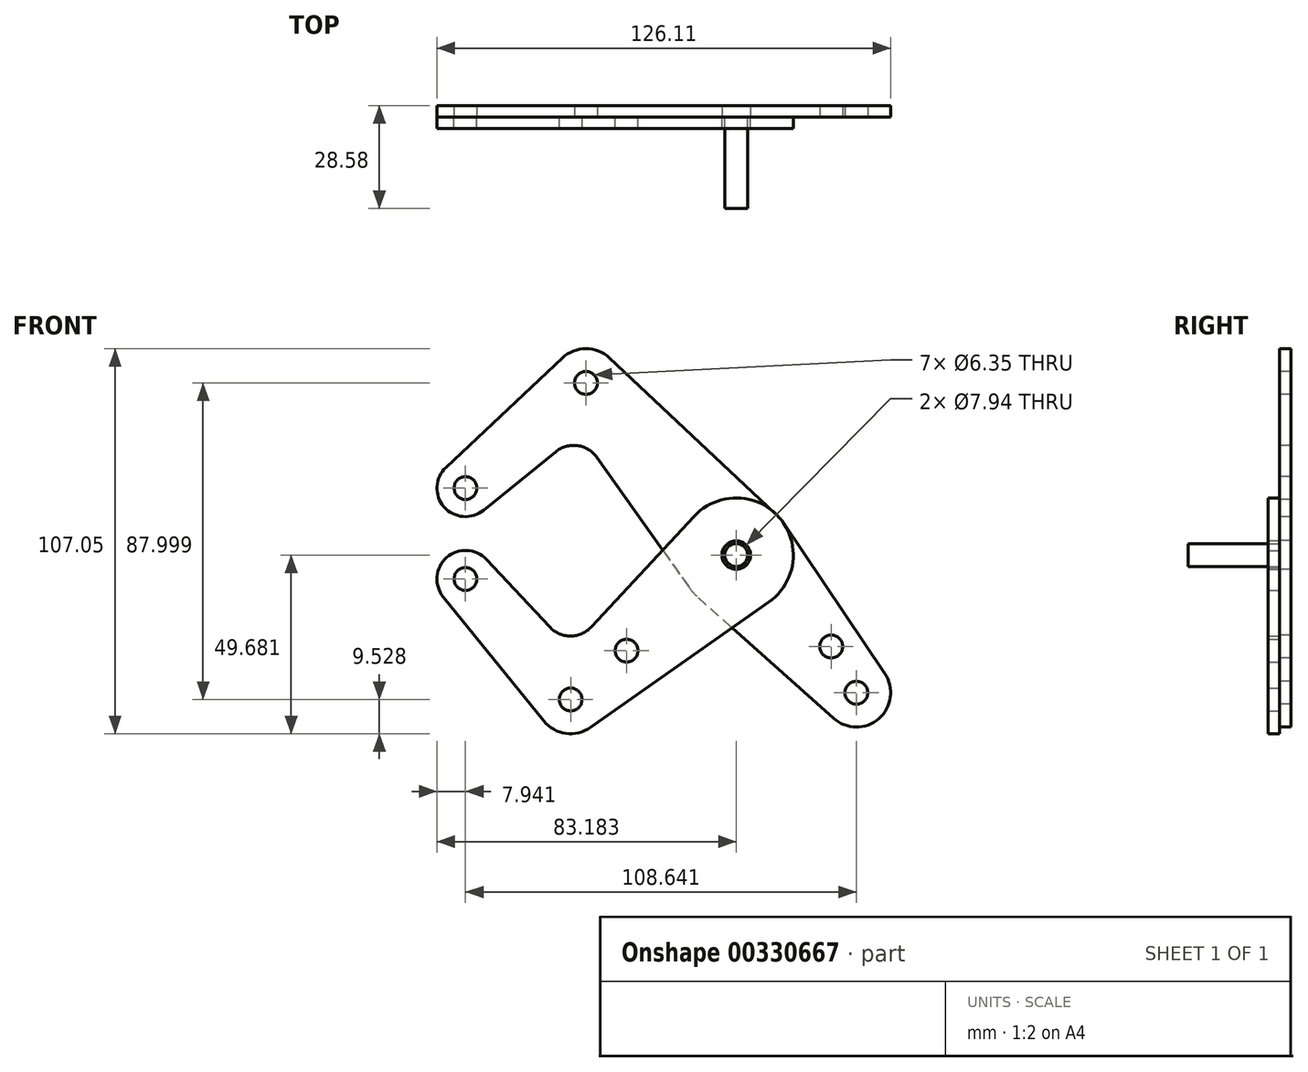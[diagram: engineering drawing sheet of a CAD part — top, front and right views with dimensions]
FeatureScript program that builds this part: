
annotation { "Feature Type Name" : "Feature", "Feature Type Description" : "" }
export const myFeature = defineFeature(function(context is Context, id is Id, definition is map)
    precondition{}
    {
        {
            var Q0;
            Q0=qCreatedBy(makeId("Front.planeOp"),FACE);
            var sketch = newSketch(context, id + "F0", { "sketchPlane" : qUnion([Q0])});
            skLineSegment(sketch, "E0", {"start": v(-8.96, 54.5) * mm, "end": v(73.88, -40.43) * mm, "construction": true});
            skCircle(sketch, "E1", {"center": v(32.8, 6.66) * mm, "radius": 3.18 * mm});
            skCircle(sketch, "E2", {"center": v(66.2, -31.62) * mm, "radius": 3.18 * mm});
            skCircle(sketch, "E3", {"center": v(-8.96, 54.5) * mm, "radius": 3.18 * mm});
            skCircle(sketch, "E4", {"center": v(-42.45, 25.28) * mm, "radius": 3.18 * mm});
            skLineSegment(sketch, "E5", {"start": v(-8.96, 54.5) * mm, "end": v(-42.45, 25.28) * mm, "construction": true});
            skCircle(sketch, "E6", {"center": v(66.2, -31.62) * mm, "radius": 9.53 * mm});
            skCircle(sketch, "E7", {"center": v(-42.45, 25.28) * mm, "radius": 7.94 * mm});
            skCircle(sketch, "E8", {"center": v(-8.96, 54.5) * mm, "radius": 9.53 * mm});
            skLineSegment(sketch, "E9", {"start": v(-47.88, 31.07) * mm, "end": v(-15.47, 61.46) * mm});
            skLineSegment(sketch, "E10", {"start": v(-37.45, 19.12) * mm, "end": v(-17.42, 35.37) * mm});
            skCircle(sketch, "E11", {"center": v(32.8, 6.66) * mm, "radius": 15.88 * mm});
            skLineSegment(sketch, "E12", {"start": v(-2.44, 61.46) * mm, "end": v(43.65, 18.24) * mm});
            skLineSegment(sketch, "E13", {"start": v(-5.94, 33.8) * mm, "end": v(19.85, -2.53) * mm});
            skLineSegment(sketch, "E14", {"start": v(22.23, -5.19) * mm, "end": v(59.85, -38.73) * mm});
            skLineSegment(sketch, "E15", {"start": v(45.97, 15.52) * mm, "end": v(74.1, -26.3) * mm});
            skArc(sketch, "E16.filletArc", {"start": v(-5.94, 33.8) * mm, "mid": v(-11.34, 37.08) * mm, "end": v(-17.42, 35.37) * mm});
            skLineSegment(sketch, "E17", {"start": v(34.62, 8.26) * mm, "end": v(-13.22, -33.5) * mm, "construction": true});
            skLineSegment(sketch, "E18", {"start": v(-13.22, -33.5) * mm, "end": v(-42.45, 0) * mm, "construction": true});
            skCircle(sketch, "E19", {"center": v(-42.45, 0) * mm, "radius": 3.18 * mm});
            skCircle(sketch, "E20", {"center": v(-13.22, -33.5) * mm, "radius": 3.18 * mm});
            skCircle(sketch, "E21", {"center": v(-42.45, 0) * mm, "radius": 7.94 * mm});
            skCircle(sketch, "E22", {"center": v(-13.22, -33.5) * mm, "radius": 9.53 * mm});
            skLineSegment(sketch, "E23", {"start": v(-36.66, 5.43) * mm, "end": v(-19.07, -13.34) * mm});
            skLineSegment(sketch, "E24", {"start": v(-48.61, -5) * mm, "end": v(-20.62, -39.5) * mm});
            skLineSegment(sketch, "E25", {"start": v(21.17, 17.47) * mm, "end": v(-7.46, -13.31) * mm});
            skLineSegment(sketch, "E26", {"start": v(41.93, -6.32) * mm, "end": v(-7.74, -41.28) * mm});
            skArc(sketch, "E27.filletArc", {"start": v(-19.07, -13.34) * mm, "mid": v(-13.26, -15.84) * mm, "end": v(-7.46, -13.31) * mm});
            skCircle(sketch, "E28", {"center": v(2.33, -19.92) * mm, "radius": 3.18 * mm});
            skCircle(sketch, "E29", {"center": v(59.2, -18.76) * mm, "radius": 3.18 * mm});
            skLineSegment(sketch, "E30", {"start": v(59.2, -18.76) * mm, "end": v(56.8, -20.85) * mm, "construction": true});
            skCircle(sketch, "E31", {"center": v(32.8, 6.66) * mm, "radius": 3.97 * mm});
            skLineSegment(sketch, "E32", {"start": v(-7.4, -25.96) * mm, "end": v(-6.39, -40.12) * mm});
            skLineSegment(sketch, "E33", {"start": v(-13.22, -33.5) * mm, "end": v(-6.9, -33.04) * mm});
            skSolve(sketch);
        }
        {
            var Q0;
            {var subQ6=sQuery(id+"F0.wireOp",EDGE,"E9");Q0=makeQuery(id+"F0.imprint","IMPRINT",FACE,{"disambiguationData":[TD([[makeQuery(id+"F0.imprint","IMPRINT",EDGE,{"derivedFrom":subQ6}),-1.0]])]});}
            var Q1;
            Q1=makeQuery(id+"F0.imprint","IMPRINT",FACE,{"disambiguationData":[TD([[makeQuery(id+"F0.imprint","IMPRINT",EDGE,{"derivedFrom":sQuery(id+"F0.wireOp",EDGE,"E3")}),-1.0]])]});
            var Q2;
            Q2=makeQuery(id+"F0.imprint","IMPRINT",FACE,{"disambiguationData":[TD([[makeQuery(id+"F0.imprint","IMPRINT",EDGE,{"derivedFrom":sQuery(id+"F0.wireOp",EDGE,"E4")}),-1.0]])]});
            var Q3;
            Q3=makeQuery(id+"F0.imprint","IMPRINT",FACE,{"disambiguationData":[TD([[makeQuery(id+"F0.imprint","IMPRINT",EDGE,{"derivedFrom":sQuery(id+"F0.wireOp",EDGE,"E31")}),-1.0]])]});
            var Q4;
            {var subQ0=sQuery(id+"F0.wireOp",EDGE,"E15");Q4=makeQuery(id+"F0.imprint","IMPRINT",FACE,{"disambiguationData":[TD([[makeQuery(id+"F0.imprint","IMPRINT",EDGE,{"derivedFrom":subQ0}),-1.0]])]});}
            var Q5;
            {var subQ0=sQuery(id+"F0.wireOp",EDGE,"E14");var subQ1=sQuery(id+"F0.wireOp",EDGE,"E11");var subQ2=makeQuery(id+"F0.imprint","INTERSECT",VERTEX,{"derivedFrom":[subQ1,subQ0]});Q5=makeQuery(id+"F0.imprint","IMPRINT",FACE,{"disambiguationData":[TD([[makeQuery(id+"F0.imprint","IMPRINT",EDGE,{"disambiguationData":[TD([[subQ2,-1.0]])],"derivedFrom":subQ1}),-1.0]])]});}
            var Q6;
            {var subQ0=sQuery(id+"F0.wireOp",EDGE,"E13");var subQ1=sQuery(id+"F0.wireOp",EDGE,"E11");var subQ2=makeQuery(id+"F0.imprint","INTERSECT",VERTEX,{"derivedFrom":[subQ1,subQ0]});Q6=makeQuery(id+"F0.imprint","IMPRINT",FACE,{"disambiguationData":[TD([[makeQuery(id+"F0.imprint","IMPRINT",EDGE,{"disambiguationData":[TD([[subQ2,1.0]])],"derivedFrom":subQ1}),-1.0]])]});}
            var Q7;
            Q7=makeQuery(id+"F0.imprint","IMPRINT",FACE,{"disambiguationData":[TD([[makeQuery(id+"F0.imprint","IMPRINT",EDGE,{"derivedFrom":sQuery(id+"F0.wireOp",EDGE,"E2")}),-1.0]])]});
            var Q8;
            {var subQ0=sQuery(id+"F0.wireOp",EDGE,"E14");var subQ1=sQuery(id+"F0.wireOp",EDGE,"E6");var subQ2=makeQuery(id+"F0.imprint","INTERSECT",VERTEX,{"derivedFrom":[subQ1,subQ0]});Q8=makeQuery(id+"F0.imprint","IMPRINT",FACE,{"disambiguationData":[TD([[makeQuery(id+"F0.imprint","IMPRINT",EDGE,{"disambiguationData":[TD([[subQ2,1.0]])],"derivedFrom":subQ1}),-1.0]])]});}
            extrude(context, id + "F1", {"entities" : qUnion([Q0, Q1, Q2, Q3, Q4, Q5, Q6, Q7, Q8]), "oppositeDirection" : true, "depth" : 3.17 * mm});
        }
        {
            var Q0;
            {var subQ13=sQuery(id+"F0.wireOp",EDGE,"E23");Q0=makeQuery(id+"F0.imprint","IMPRINT",FACE,{"disambiguationData":[TD([[makeQuery(id+"F0.imprint","IMPRINT",EDGE,{"derivedFrom":subQ13}),-1.0]])]});}
            var Q1;
            Q1=makeQuery(id+"F0.imprint","IMPRINT",FACE,{"disambiguationData":[TD([[makeQuery(id+"F0.imprint","IMPRINT",EDGE,{"derivedFrom":sQuery(id+"F0.wireOp",EDGE,"E20")}),-1.0]])]});
            var Q2;
            Q2=makeQuery(id+"F0.imprint","IMPRINT",FACE,{"disambiguationData":[TD([[makeQuery(id+"F0.imprint","IMPRINT",EDGE,{"derivedFrom":sQuery(id+"F0.wireOp",EDGE,"E19")}),-1.0]])]});
            var Q3;
            {var subQ0=sQuery(id+"F0.wireOp",EDGE,"E14");var subQ1=sQuery(id+"F0.wireOp",EDGE,"E11");var subQ2=makeQuery(id+"F0.imprint","INTERSECT",VERTEX,{"derivedFrom":[subQ1,subQ0]});Q3=makeQuery(id+"F0.imprint","IMPRINT",FACE,{"disambiguationData":[TD([[makeQuery(id+"F0.imprint","IMPRINT",EDGE,{"disambiguationData":[TD([[subQ2,-1.0]])],"derivedFrom":subQ1}),-1.0]])]});}
            var Q4;
            Q4=makeQuery(id+"F0.imprint","IMPRINT",FACE,{"disambiguationData":[TD([[makeQuery(id+"F0.imprint","IMPRINT",EDGE,{"derivedFrom":sQuery(id+"F0.wireOp",EDGE,"E31")}),-1.0]])]});
            var Q5;
            {var subQ0=sQuery(id+"F0.wireOp",EDGE,"E13");var subQ1=sQuery(id+"F0.wireOp",EDGE,"E11");var subQ2=makeQuery(id+"F0.imprint","INTERSECT",VERTEX,{"derivedFrom":[subQ1,subQ0]});Q5=makeQuery(id+"F0.imprint","IMPRINT",FACE,{"disambiguationData":[TD([[makeQuery(id+"F0.imprint","IMPRINT",EDGE,{"disambiguationData":[TD([[subQ2,1.0]])],"derivedFrom":subQ1}),-1.0]])]});}
            var Q6;
            {var subQ0=sQuery(id+"F0.wireOp",EDGE,"ZGzwKxSN-V8be-wxfP-rIrm-HyRwKm10lSNJ");var subQ1=sQuery(id+"F0.wireOp",EDGE,"E22");var subQ2=makeQuery(id+"F0.imprint","INTERSECT",VERTEX,{"disambiguationData":[OD(0.0)],"derivedFrom":[subQ1,subQ0]});Q6=makeQuery(id+"F0.imprint","IMPRINT",FACE,{"disambiguationData":[TD([[makeQuery(id+"F0.imprint","IMPRINT",EDGE,{"disambiguationData":[TD([[subQ2,1.0]])],"derivedFrom":subQ1}),1.0]])]});}
            var Q7;
            {var subQ0=sQuery(id+"F0.wireOp",EDGE,"ZGzwKxSN-V8be-wxfP-rIrm-HyRwKm10lSNJ");var subQ1=sQuery(id+"F0.wireOp",EDGE,"E22");var subQ2=makeQuery(id+"F0.imprint","INTERSECT",VERTEX,{"disambiguationData":[OD(1.0)],"derivedFrom":[subQ1,subQ0]});Q7=makeQuery(id+"F0.imprint","IMPRINT",FACE,{"disambiguationData":[TD([[makeQuery(id+"F0.imprint","IMPRINT",EDGE,{"disambiguationData":[TD([[subQ2,-1.0]])],"derivedFrom":subQ1}),1.0]])]});}
            var Q8;
            {var subQ0=sQuery(id+"F0.wireOp",EDGE,"E26");var subQ1=sQuery(id+"F0.wireOp",EDGE,"E22");var subQ2=makeQuery(id+"F0.imprint","INTERSECT",VERTEX,{"derivedFrom":[subQ1,subQ0]});Q8=makeQuery(id+"F0.imprint","IMPRINT",FACE,{"disambiguationData":[TD([[makeQuery(id+"F0.imprint","IMPRINT",EDGE,{"disambiguationData":[TD([[subQ2,-1.0]])],"derivedFrom":subQ1}),-1.0]])]});}
            var Q9;
            {var subQ0=sQuery(id+"F0.wireOp",EDGE,"E32");var subQ4=makeQuery(id+"F0.imprint","IMPRINT",VERTEX,{"derivedFrom":subQ0});Q9=makeQuery(id+"F0.imprint","IMPRINT",FACE,{"disambiguationData":[TD([[makeQuery(id+"F0.imprint","IMPRINT",EDGE,{"disambiguationData":[TD([[subQ4,1.0]])],"derivedFrom":subQ0}),1.0]])]});}
            extrude(context, id + "F2", {"entities" : qUnion([Q0, Q1, Q2, Q3, Q4, Q5, Q6, Q7, Q8, Q9]), "depth" : 3.17 * mm});
        }
        {
            var Q0;
            Q0=makeQuery(id+"F0.imprint","IMPRINT",FACE,{"disambiguationData":[TD([[makeQuery(id+"F0.imprint","IMPRINT",EDGE,{"derivedFrom":sQuery(id+"F0.wireOp",EDGE,"E1")}),1.0]])]});
            extrude(context, id + "F3", {"entities" : qUnion([Q0]), "depth" : 25.4 * mm});
        }
    });
